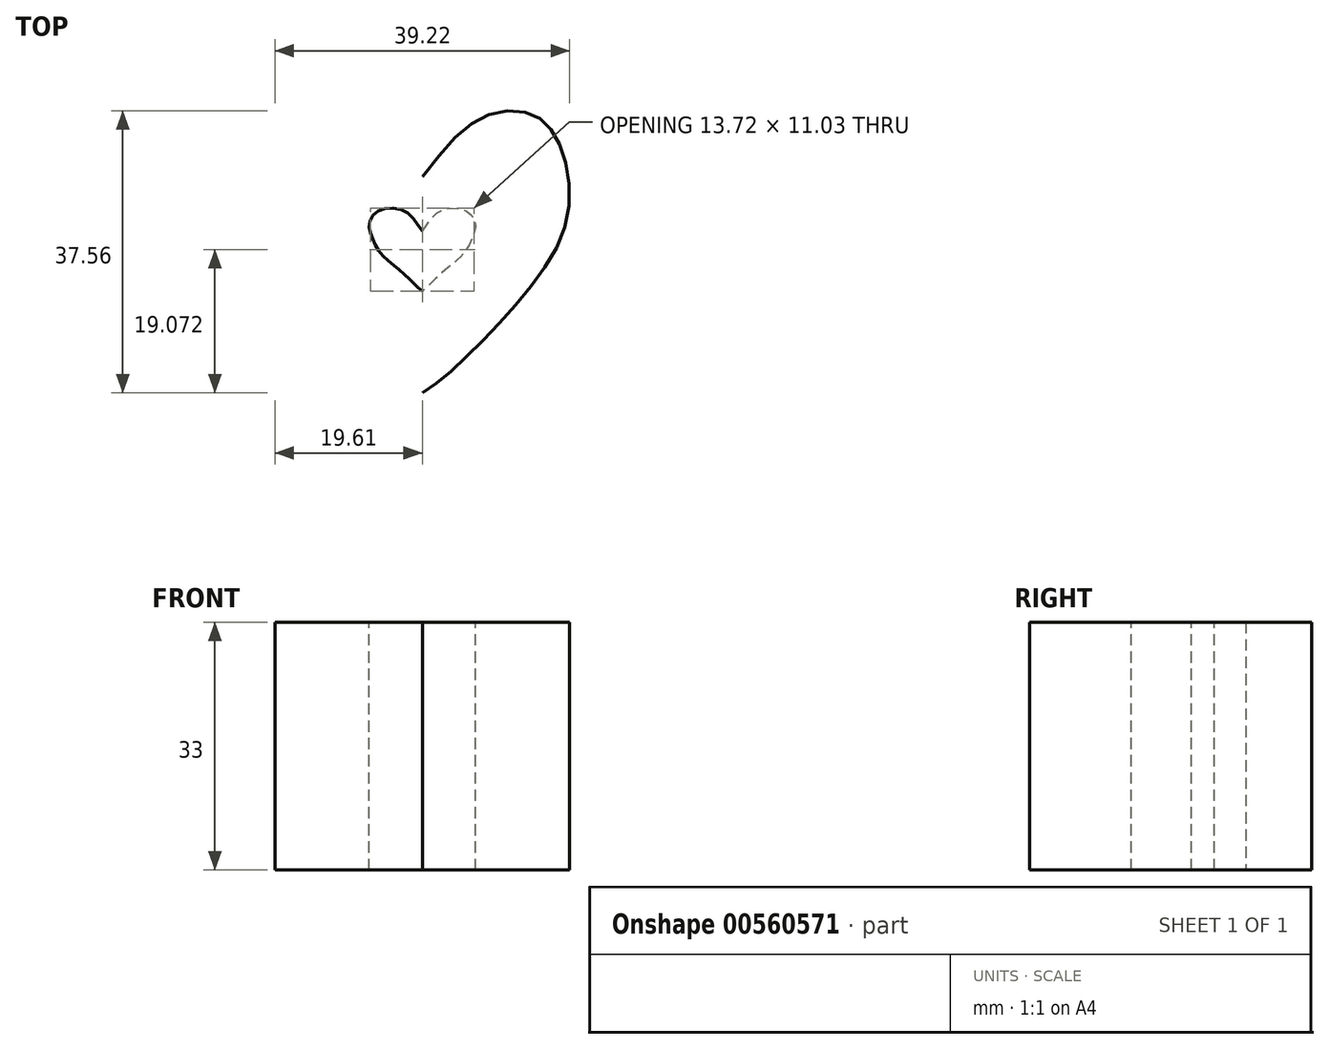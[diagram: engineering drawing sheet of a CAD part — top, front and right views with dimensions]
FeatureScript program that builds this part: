
annotation { "Feature Type Name" : "Feature", "Feature Type Description" : "" }
export const myFeature = defineFeature(function(context is Context, id is Id, definition is map)
    precondition{}
    {
        {
            var Q0;
            Q0=qCreatedBy(makeId("Top.planeOp"),FACE);
            var sketch = newSketch(context, id + "F0", { "sketchPlane" : qUnion([Q0])});
            skFitSpline(sketch, "E0", {"points": [v(0, 10.25) * mm, v(8.19, 18.25) * mm, v(14.83, 18.44) * mm, v(18.35, 14.34) * mm, v(19.36, 5.03) * mm, v(14.25, -4.59) * mm, v(6.05, -13.56) * mm, v(0, -18.53) * mm], "startDerivative": vector(53.63, 68.38) * mm, "endDerivative": vector(-42.6, -24.21) * mm});
            skLineSegment(sketch, "E1", {"start": v(0, 10.25) * mm, "end": v(0, -9.36) * mm, "construction": true});
            skFitSpline(sketch, "E2.MirrorCS", {"points": [v(0, 10.25) * mm, v(-8.19, 18.25) * mm, v(-14.83, 18.44) * mm, v(-18.35, 14.34) * mm, v(-19.36, 5.03) * mm, v(-14.25, -4.59) * mm, v(-6.05, -13.56) * mm, v(0, -18.53) * mm], "startDerivative": vector(-53.63, 68.38) * mm, "endDerivative": vector(42.6, -24.21) * mm});
            skSolve(sketch);
        }
        {
            var Q0;
            {var subQ1=sQuery(id+"F0.wireOp",EDGE,"E0");var subQ3=sQuery(id+"F0.wireOp",EDGE,"rDdCRVCM-XOSB-dXGY-6ydD-Vg9bKhy9GweG");var subQ6=makeQuery(id+"F0.imprint","INTERSECT",VERTEX,{"disambiguationData":[OD(0.0)],"derivedFrom":[subQ3,subQ1]});Q0=makeQuery(id+"F0.imprint","IMPRINT",FACE,{"disambiguationData":[TD([[makeQuery(id+"F0.imprint","IMPRINT",EDGE,{"disambiguationData":[TD([[subQ6,1.0]])],"derivedFrom":subQ3}),1.0]])]});}
            var Q1;
            {var subQ0=sQuery(id+"F0.wireOp",EDGE,"E2.MirrorCS");var subQ1=sQuery(id+"F0.wireOp",EDGE,"rDdCRVCM-XOSB-dXGY-6ydD-Vg9bKhy9GweG");var subQ2=makeQuery(id+"F0.imprint","INTERSECT",VERTEX,{"disambiguationData":[OD(0.0)],"derivedFrom":[subQ1,subQ0]});Q1=makeQuery(id+"F0.imprint","IMPRINT",FACE,{"disambiguationData":[TD([[makeQuery(id+"F0.imprint","IMPRINT",EDGE,{"disambiguationData":[TD([[subQ2,-1.0]])],"derivedFrom":subQ1}),-1.0]])]});}
            var Q2;
            {var subQ0=sQuery(id+"F0.wireOp",EDGE,"E0");var subQ1=sQuery(id+"F0.wireOp",EDGE,"rDdCRVCM-XOSB-dXGY-6ydD-Vg9bKhy9GweG");var subQ2=makeQuery(id+"F0.imprint","INTERSECT",VERTEX,{"disambiguationData":[OD(0.0)],"derivedFrom":[subQ1,subQ0]});Q2=makeQuery(id+"F0.imprint","IMPRINT",FACE,{"disambiguationData":[TD([[makeQuery(id+"F0.imprint","IMPRINT",EDGE,{"disambiguationData":[TD([[subQ2,1.0]])],"derivedFrom":subQ1}),-1.0]])]});}
            var Q3;
            Q3=makeQuery(id+"F0.imprint","IMPRINT",FACE,{"disambiguationData":[TD([[makeQuery(id+"F0.imprint","IMPRINT",EDGE,{"derivedFrom":sQuery(id+"F0.wireOp",EDGE,"E0")}),-1.0]])]});
            extrude(context, id + "F1", {"entities" : qUnion([Q0, Q1, Q2, Q3]), "depth" : 33 * mm, "offsetDistance" : 25 * mm});
        }
        {
            var Q0;
            Q0=makeQuery(id+"F1.opExtrude","CAP_FACE",FACE,{"disambiguationData":[OSD([sQuery(id+"F0.wireOp",EDGE,"E0"),sQuery(id+"F0.wireOp",EDGE,"E2.MirrorCS")])],"isStart":false});
            var sketch = newSketch(context, id + "F2", { "sketchPlane" : qUnion([Q0])});
            skSolve(sketch);
        }
        {
            var Q0;
            Q0=makeQuery(id+"F2.imprint","IMPRINT",FACE,{"disambiguationData":[TD([[makeQuery(id+"F2.imprint","IMPRINT",EDGE,{"derivedFrom":makeQuery(id+"F1.opExtrude","CAP_EDGE",EDGE,{"disambiguationData":[OSD([sQuery(id+"F0.wireOp",EDGE,"E0")])],"isStart":false})}),-1.0]])]});
            var sketch = newSketch(context, id + "F3", { "sketchPlane" : qUnion([Q0])});
            skFitSpline(sketch, "E3", {"points": [v(0, 3.03) * mm, v(2.15, 5.57) * mm, v(5.46, 5.86) * mm, v(7.03, 4.2) * mm, v(6.64, 2.05) * mm, v(5.46, 0) * mm, v(3.32, -1.95) * mm, v(1.37, -3.7) * mm, v(0, -4.97) * mm], "startDerivative": vector(13.38, 17.29) * mm, "endDerivative": vector(-11.6, -7.37) * mm});
            skFitSpline(sketch, "E4.MirrorCS", {"points": [v(0, 3.03) * mm, v(-2.15, 5.57) * mm, v(-5.46, 5.86) * mm, v(-7.03, 4.2) * mm, v(-6.64, 2.05) * mm, v(-5.46, 0) * mm, v(-3.32, -1.95) * mm, v(-1.37, -3.7) * mm, v(0, -4.97) * mm], "startDerivative": vector(-13.38, 17.29) * mm, "endDerivative": vector(11.6, -7.37) * mm});
            skSolve(sketch);
        }
        {
            var Q0;
            Q0 = qSketchRegion(id + "F3", true);
            extrude(context, id + "F4", {"entities" : qUnion([Q0]), "operationType" : NewBodyOperationType.REMOVE, "oppositeDirection" : true, "depth" : 76.9 * mm, "offsetDistance" : 25 * mm});
        }
    });
